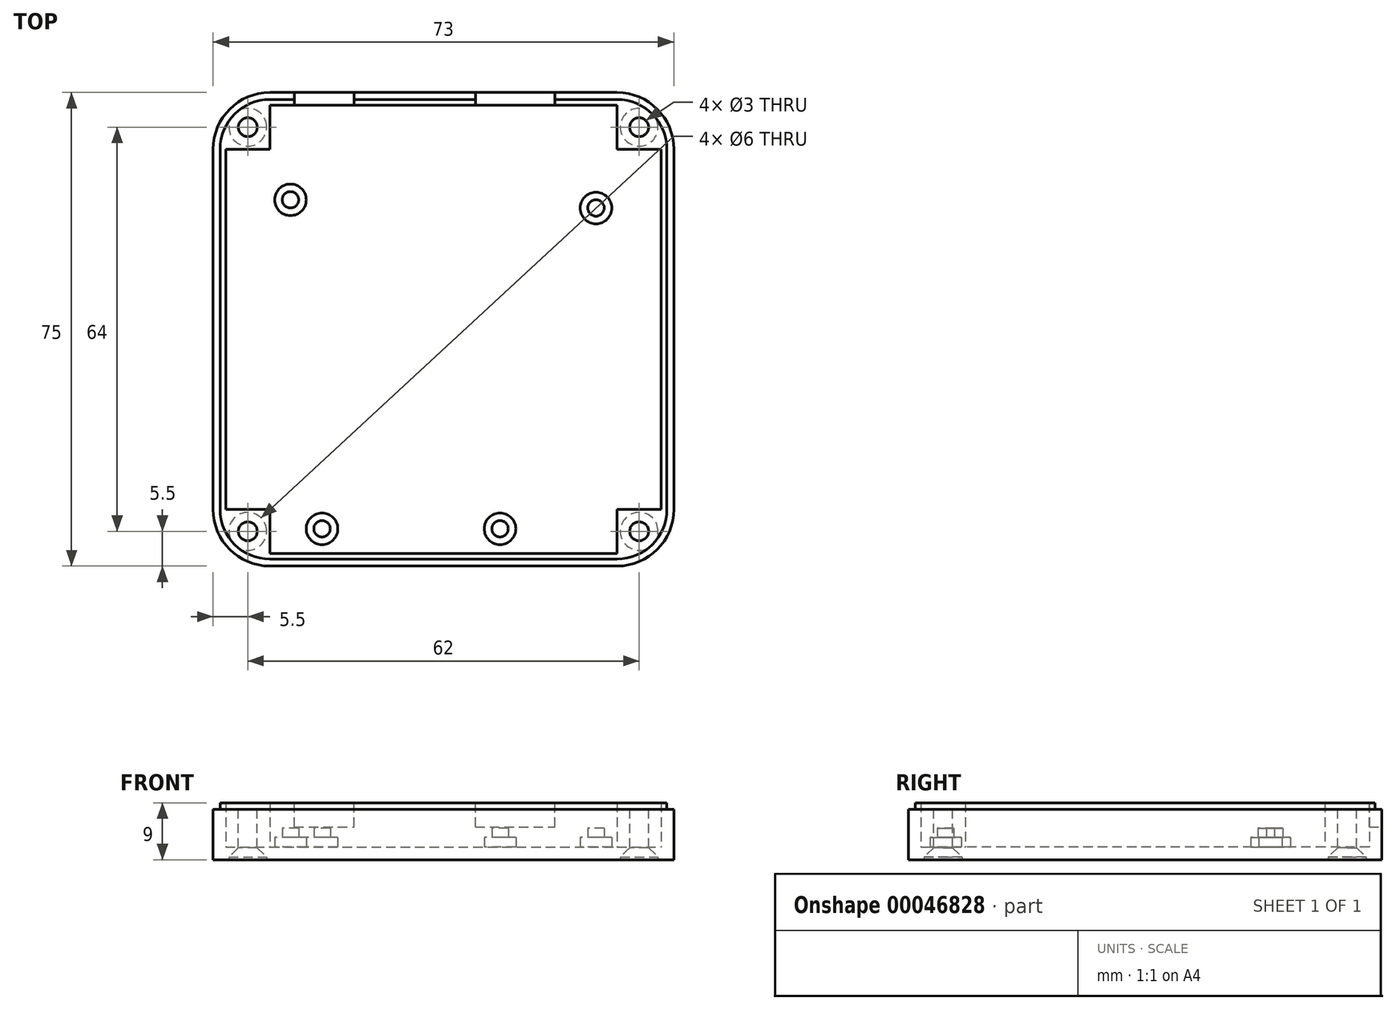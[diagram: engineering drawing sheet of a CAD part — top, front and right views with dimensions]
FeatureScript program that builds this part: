
annotation { "Feature Type Name" : "Feature", "Feature Type Description" : "" }
export const myFeature = defineFeature(function(context is Context, id is Id, definition is map)
    precondition{}
    {
        {
            var Q0;
            Q0=qCreatedBy(makeId("Top.planeOp"),FACE);
            var sketch = newSketch(context, id + "F0", { "sketchPlane" : qUnion([Q0])});
            skLineSegment(sketch, "E0.bottom", {"start": v(-27.5, 38.5) * mm, "end": v(27.5, 38.5) * mm});
            skLineSegment(sketch, "E0.top", {"start": v(-27.5, -36.5) * mm, "end": v(27.5, -36.5) * mm});
            skLineSegment(sketch, "E0.left", {"start": v(-36.5, 29.5) * mm, "end": v(-36.5, -27.5) * mm});
            skLineSegment(sketch, "E0.right", {"start": v(36.5, 29.5) * mm, "end": v(36.5, -27.5) * mm});
            skPoint(sketch, "E1.visualSharp", {"position": v(-36.5, 38.5) * mm});
            skArc(sketch, "E1.filletArc", {"start": v(-27.5, 38.5) * mm, "mid": v(-33.86, 35.86) * mm, "end": v(-36.5, 29.5) * mm});
            skPoint(sketch, "E2.visualSharp", {"position": v(36.5, 38.5) * mm});
            skArc(sketch, "E2.filletArc", {"start": v(36.5, 29.5) * mm, "mid": v(33.86, 35.86) * mm, "end": v(27.5, 38.5) * mm});
            skPoint(sketch, "E3.visualSharp", {"position": v(36.5, -36.5) * mm});
            skArc(sketch, "E3.filletArc", {"start": v(27.5, -36.5) * mm, "mid": v(33.86, -33.86) * mm, "end": v(36.5, -27.5) * mm});
            skPoint(sketch, "E4.visualSharp", {"position": v(-36.5, -36.5) * mm});
            skArc(sketch, "E4.filletArc", {"start": v(-36.5, -27.5) * mm, "mid": v(-33.86, -33.86) * mm, "end": v(-27.5, -36.5) * mm});
            skSolve(sketch);
        }
        {
            var Q0;
            Q0 = qSketchRegion(id + "F0", true);
            extrude(context, id + "F1", {"entities" : qUnion([Q0]), "depth" : 2 * mm});
        }
        {
            var Q0;
            Q0=makeQuery(id+"F1.opExtrude","CAP_FACE",FACE,{"disambiguationData":[OSD([sQuery(id+"F0.wireOp",EDGE,"E0.bottom"),sQuery(id+"F0.wireOp",EDGE,"E0.top"),sQuery(id+"F0.wireOp",EDGE,"E0.left"),sQuery(id+"F0.wireOp",EDGE,"E0.right")])],"isStart":false});
            var sketch = newSketch(context, id + "F2", { "sketchPlane" : qUnion([Q0])});
            skCircle(sketch, "E5", {"center": v(-19.24, -30.6) * mm, "radius": 2.5 * mm});
            skCircle(sketch, "E6", {"center": v(8.96, -30.6) * mm, "radius": 2.5 * mm});
            skCircle(sketch, "E7", {"center": v(24.16, 20.2) * mm, "radius": 2.5 * mm});
            skCircle(sketch, "E8", {"center": v(-24.24, 21.5) * mm, "radius": 2.5 * mm});
            skSolve(sketch);
        }
        {
            var Q0;
            Q0 = qSketchRegion(id + "F2", true);
            extrude(context, id + "F3", {"entities" : qUnion([Q0]), "operationType" : NewBodyOperationType.ADD, "depth" : 1.5 * mm});
        }
        {
            var Q0;
            Q0=makeQuery(id+"F3.opExtrude","CAP_FACE",FACE,{"disambiguationData":[OSD([sQuery(id+"F2.wireOp",EDGE,"E8")])],"isStart":false});
            var sketch = newSketch(context, id + "F4", { "sketchPlane" : qUnion([Q0])});
            skCircle(sketch, "E9", {"center": v(-19.24, -30.6) * mm, "radius": 1.3 * mm});
            skCircle(sketch, "E10", {"center": v(8.96, -30.6) * mm, "radius": 1.3 * mm});
            skCircle(sketch, "E11", {"center": v(24.16, 20.2) * mm, "radius": 1.3 * mm});
            skCircle(sketch, "E12", {"center": v(-24.24, 21.5) * mm, "radius": 1.3 * mm});
            skSolve(sketch);
        }
        {
            var Q0;
            Q0 = qSketchRegion(id + "F4", true);
            extrude(context, id + "F5", {"entities" : qUnion([Q0]), "operationType" : NewBodyOperationType.ADD, "depth" : 1.5 * mm});
        }
        {
            var Q0;
            Q0=makeQuery(id+"F1.opExtrude","CAP_FACE",FACE,{"disambiguationData":[OSD([sQuery(id+"F0.wireOp",EDGE,"E0.bottom"),sQuery(id+"F0.wireOp",EDGE,"E0.top"),sQuery(id+"F0.wireOp",EDGE,"E0.left"),sQuery(id+"F0.wireOp",EDGE,"E0.right"),sQuery(id+"F0.wireOp",EDGE,"E1.filletArc"),sQuery(id+"F0.wireOp",EDGE,"E2.filletArc"),sQuery(id+"F0.wireOp",EDGE,"E3.filletArc"),sQuery(id+"F0.wireOp",EDGE,"E4.filletArc")])],"isStart":false});
            var sketch = newSketch(context, id + "F6", { "sketchPlane" : qUnion([Q0])});
            skLineSegment(sketch, "E13.bottom", {"start": v(-27.5, 38.5) * mm, "end": v(27.5, 38.5) * mm});
            skLineSegment(sketch, "E13.top", {"start": v(-27.5, -36.5) * mm, "end": v(27.5, -36.5) * mm});
            skLineSegment(sketch, "E13.left", {"start": v(-36.5, 29.5) * mm, "end": v(-36.5, -27.5) * mm});
            skLineSegment(sketch, "E13.right", {"start": v(36.5, 29.5) * mm, "end": v(36.5, -27.5) * mm});
            skPoint(sketch, "E14.visualSharp", {"position": v(-36.5, 38.5) * mm});
            skArc(sketch, "E14.filletArc", {"start": v(-27.5, 38.5) * mm, "mid": v(-33.86, 35.86) * mm, "end": v(-36.5, 29.5) * mm});
            skPoint(sketch, "E15.visualSharp", {"position": v(36.5, 38.5) * mm});
            skArc(sketch, "E15.filletArc", {"start": v(36.5, 29.5) * mm, "mid": v(33.86, 35.86) * mm, "end": v(27.5, 38.5) * mm});
            skPoint(sketch, "E16.visualSharp", {"position": v(36.5, -36.5) * mm});
            skArc(sketch, "E16.filletArc", {"start": v(27.5, -36.5) * mm, "mid": v(33.86, -33.86) * mm, "end": v(36.5, -27.5) * mm});
            skPoint(sketch, "E17.visualSharp", {"position": v(-36.5, -36.5) * mm});
            skArc(sketch, "E17.filletArc", {"start": v(-36.5, -27.5) * mm, "mid": v(-33.86, -33.86) * mm, "end": v(-27.5, -36.5) * mm});
            skLineSegment(sketch, "E18", {"start": v(-27.5, 36.5) * mm, "end": v(27.5, 36.5) * mm});
            skLineSegment(sketch, "E19", {"start": v(-34.5, 29.5) * mm, "end": v(-34.5, -27.5) * mm});
            skLineSegment(sketch, "E20", {"start": v(-27.5, -34.5) * mm, "end": v(27.5, -34.5) * mm});
            skLineSegment(sketch, "E21", {"start": v(34.5, 29.5) * mm, "end": v(34.5, -27.5) * mm});
            skLineSegment(sketch, "E22", {"start": v(-34.5, 29.5) * mm, "end": v(-27.5, 29.5) * mm});
            skLineSegment(sketch, "E23", {"start": v(-27.5, 36.5) * mm, "end": v(-27.5, 29.5) * mm});
            skLineSegment(sketch, "E24", {"start": v(27.5, 36.5) * mm, "end": v(27.5, 29.5) * mm});
            skLineSegment(sketch, "E25", {"start": v(27.5, 29.5) * mm, "end": v(34.5, 29.5) * mm});
            skLineSegment(sketch, "E26", {"start": v(-34.5, -27.5) * mm, "end": v(-27.5, -27.5) * mm});
            skLineSegment(sketch, "E27", {"start": v(-27.5, -34.5) * mm, "end": v(-27.5, -27.5) * mm});
            skLineSegment(sketch, "E28", {"start": v(27.5, -34.5) * mm, "end": v(27.5, -27.5) * mm});
            skLineSegment(sketch, "E29", {"start": v(27.5, -27.5) * mm, "end": v(34.5, -27.5) * mm});
            skSolve(sketch);
        }
        {
            var Q0;
            Q0 = qSketchRegion(id + "F6", true);
            extrude(context, id + "F7", {"entities" : qUnion([Q0]), "operationType" : NewBodyOperationType.ADD, "depth" : 7 * mm});
        }
        {
            var Q0;
            Q0=makeQuery(id+"F7.opExtrude","CAP_FACE",FACE,{"disambiguationData":[OSD([sQuery(id+"F6.wireOp",EDGE,"E13.bottom"),sQuery(id+"F6.wireOp",EDGE,"E13.top"),sQuery(id+"F6.wireOp",EDGE,"E13.left"),sQuery(id+"F6.wireOp",EDGE,"E13.right"),sQuery(id+"F6.wireOp",EDGE,"E14.filletArc"),sQuery(id+"F6.wireOp",EDGE,"E15.filletArc"),sQuery(id+"F6.wireOp",EDGE,"E16.filletArc"),sQuery(id+"F6.wireOp",EDGE,"E17.filletArc"),sQuery(id+"F6.wireOp",EDGE,"E18"),sQuery(id+"F6.wireOp",EDGE,"E19"),sQuery(id+"F6.wireOp",EDGE,"E20"),sQuery(id+"F6.wireOp",EDGE,"E21"),sQuery(id+"F6.wireOp",EDGE,"E22"),sQuery(id+"F6.wireOp",EDGE,"E23"),sQuery(id+"F6.wireOp",EDGE,"E24"),sQuery(id+"F6.wireOp",EDGE,"E25"),sQuery(id+"F6.wireOp",EDGE,"E26"),sQuery(id+"F6.wireOp",EDGE,"E27"),sQuery(id+"F6.wireOp",EDGE,"E28"),sQuery(id+"F6.wireOp",EDGE,"E29")])],"isStart":false});
            var sketch = newSketch(context, id + "F8", { "sketchPlane" : qUnion([Q0])});
            skCircle(sketch, "E30", {"center": v(-31, 33) * mm, "radius": 1.5 * mm});
            skCircle(sketch, "E31", {"center": v(31, 33) * mm, "radius": 1.5 * mm});
            skCircle(sketch, "E32", {"center": v(-31, -31) * mm, "radius": 1.5 * mm});
            skCircle(sketch, "E33", {"center": v(31, -31) * mm, "radius": 1.5 * mm});
            skSolve(sketch);
        }
        {
            var Q0;
            Q0 = qSketchRegion(id + "F8", true);
            extrude(context, id + "F9", {"entities" : qUnion([Q0]), "operationType" : NewBodyOperationType.REMOVE, "oppositeDirection" : true, "depth" : 10 * mm});
        }
        {
            var Q0;
            Q0=makeQuery(id+"F7.opExtrude","CAP_FACE",FACE,{"disambiguationData":[OSD([sQuery(id+"F6.wireOp",EDGE,"E13.bottom"),sQuery(id+"F6.wireOp",EDGE,"E13.top"),sQuery(id+"F6.wireOp",EDGE,"E13.left"),sQuery(id+"F6.wireOp",EDGE,"E13.right"),sQuery(id+"F6.wireOp",EDGE,"E14.filletArc"),sQuery(id+"F6.wireOp",EDGE,"E15.filletArc"),sQuery(id+"F6.wireOp",EDGE,"E16.filletArc"),sQuery(id+"F6.wireOp",EDGE,"E17.filletArc"),sQuery(id+"F6.wireOp",EDGE,"E18"),sQuery(id+"F6.wireOp",EDGE,"E19"),sQuery(id+"F6.wireOp",EDGE,"E20"),sQuery(id+"F6.wireOp",EDGE,"E21"),sQuery(id+"F6.wireOp",EDGE,"E22"),sQuery(id+"F6.wireOp",EDGE,"E23"),sQuery(id+"F6.wireOp",EDGE,"E24"),sQuery(id+"F6.wireOp",EDGE,"E25"),sQuery(id+"F6.wireOp",EDGE,"E26"),sQuery(id+"F6.wireOp",EDGE,"E27"),sQuery(id+"F6.wireOp",EDGE,"E28"),sQuery(id+"F6.wireOp",EDGE,"E29")])],"isStart":false});
            var sketch = newSketch(context, id + "F10", { "sketchPlane" : qUnion([Q0])});
            skLineSegment(sketch, "E34.bottom", {"start": v(17.66, 36.5) * mm, "end": v(5.06, 36.5) * mm});
            skLineSegment(sketch, "E34.top", {"start": v(17.66, 38.5) * mm, "end": v(5.06, 38.5) * mm});
            skLineSegment(sketch, "E34.left", {"start": v(17.66, 36.5) * mm, "end": v(17.66, 38.5) * mm});
            skLineSegment(sketch, "E34.right", {"start": v(5.06, 36.5) * mm, "end": v(5.06, 38.5) * mm});
            skLineSegment(sketch, "E35.bottom", {"start": v(-14.14, 36.5) * mm, "end": v(-23.64, 36.5) * mm});
            skLineSegment(sketch, "E35.top", {"start": v(-14.14, 38.5) * mm, "end": v(-23.64, 38.5) * mm});
            skLineSegment(sketch, "E35.left", {"start": v(-14.14, 36.5) * mm, "end": v(-14.14, 38.5) * mm});
            skLineSegment(sketch, "E35.right", {"start": v(-23.64, 36.5) * mm, "end": v(-23.64, 38.5) * mm});
            skSolve(sketch);
        }
        {
            var Q0;
            Q0 = qSketchRegion(id + "F10", true);
            extrude(context, id + "F11", {"entities" : qUnion([Q0]), "operationType" : NewBodyOperationType.REMOVE, "oppositeDirection" : true, "depth" : 3.8 * mm});
        }
        {
            var Q0;
            Q0=makeQuery(id+"F1.opExtrude","CAP_FACE",FACE,{"disambiguationData":[OSD([sQuery(id+"F0.wireOp",EDGE,"E0.bottom"),sQuery(id+"F0.wireOp",EDGE,"E0.top"),sQuery(id+"F0.wireOp",EDGE,"E0.left"),sQuery(id+"F0.wireOp",EDGE,"E0.right"),sQuery(id+"F0.wireOp",EDGE,"E1.filletArc"),sQuery(id+"F0.wireOp",EDGE,"E2.filletArc"),sQuery(id+"F0.wireOp",EDGE,"E3.filletArc"),sQuery(id+"F0.wireOp",EDGE,"E4.filletArc")])],"isStart":true});
            var sketch = newSketch(context, id + "F12", { "sketchPlane" : qUnion([Q0])});
            skCircle(sketch, "E36", {"center": v(31, -33) * mm, "radius": 3 * mm});
            skCircle(sketch, "E37", {"center": v(-31, -33) * mm, "radius": 3 * mm});
            skCircle(sketch, "E38", {"center": v(-31, 31) * mm, "radius": 3 * mm});
            skCircle(sketch, "E39", {"center": v(31, 31) * mm, "radius": 3 * mm});
            skSolve(sketch);
        }
        {
            var Q0;
            Q0 = qSketchRegion(id + "F12", true);
            extrude(context, id + "F13", {"entities" : qUnion([Q0]), "operationType" : NewBodyOperationType.REMOVE, "oppositeDirection" : true, "depth" : .4 * mm});
        }
        {
            var Q0;
            Q0=makeQuery(id+"F13.boolean.opBoolean","INTERSECT",EDGE,{"derivedFrom":[makeQuery(id+"F9.boolean.opBoolean","COPY",FACE,{"derivedFrom":makeQuery(id+"F9.opExtrude","SWEPT_FACE",FACE,{"disambiguationData":[OSD([sQuery(id+"F8.wireOp",EDGE,"E31")])]})}),makeQuery(id+"F13.opExtrude","CAP_FACE",FACE,{"disambiguationData":[OSD([sQuery(id+"F12.wireOp",EDGE,"E36")])],"isStart":false})]});
            var Q1;
            Q1=makeQuery(id+"F13.boolean.opBoolean","INTERSECT",EDGE,{"derivedFrom":[makeQuery(id+"F9.boolean.opBoolean","COPY",FACE,{"derivedFrom":makeQuery(id+"F9.opExtrude","SWEPT_FACE",FACE,{"disambiguationData":[OSD([sQuery(id+"F8.wireOp",EDGE,"E30")])]})}),makeQuery(id+"F13.opExtrude","CAP_FACE",FACE,{"disambiguationData":[OSD([sQuery(id+"F12.wireOp",EDGE,"E37")])],"isStart":false})]});
            var Q2;
            Q2=makeQuery(id+"F13.boolean.opBoolean","INTERSECT",EDGE,{"derivedFrom":[makeQuery(id+"F9.boolean.opBoolean","COPY",FACE,{"derivedFrom":makeQuery(id+"F9.opExtrude","SWEPT_FACE",FACE,{"disambiguationData":[OSD([sQuery(id+"F8.wireOp",EDGE,"E33")])]})}),makeQuery(id+"F13.opExtrude","CAP_FACE",FACE,{"disambiguationData":[OSD([sQuery(id+"F12.wireOp",EDGE,"E39")])],"isStart":false})]});
            var Q3;
            Q3=makeQuery(id+"F13.boolean.opBoolean","INTERSECT",EDGE,{"derivedFrom":[makeQuery(id+"F9.boolean.opBoolean","COPY",FACE,{"derivedFrom":makeQuery(id+"F9.opExtrude","SWEPT_FACE",FACE,{"disambiguationData":[OSD([sQuery(id+"F8.wireOp",EDGE,"E32")])]})}),makeQuery(id+"F13.opExtrude","CAP_FACE",FACE,{"disambiguationData":[OSD([sQuery(id+"F12.wireOp",EDGE,"E38")])],"isStart":false})]});
            chamfer(context, id + "F14", {"entities" : qUnion([Q0, Q1, Q2, Q3]), "width" : 1.5 * mm, "tangentPropagation" : true});
        }
        {
            var Q0;
            {var subQ0=sQuery(id+"F6.wireOp",EDGE,"E13.bottom");var subQ1=sQuery(id+"F6.wireOp",EDGE,"E13.top");var subQ2=sQuery(id+"F6.wireOp",EDGE,"E13.left");var subQ3=sQuery(id+"F6.wireOp",EDGE,"E13.right");var subQ4=sQuery(id+"F6.wireOp",EDGE,"E14.filletArc");var subQ5=sQuery(id+"F6.wireOp",EDGE,"E15.filletArc");var subQ6=sQuery(id+"F6.wireOp",EDGE,"E16.filletArc");var subQ7=sQuery(id+"F6.wireOp",EDGE,"E17.filletArc");var subQ8=sQuery(id+"F6.wireOp",EDGE,"E18");var subQ9=sQuery(id+"F6.wireOp",EDGE,"E19");var subQ10=sQuery(id+"F6.wireOp",EDGE,"E20");var subQ11=sQuery(id+"F6.wireOp",EDGE,"E21");var subQ12=sQuery(id+"F6.wireOp",EDGE,"E22");var subQ13=sQuery(id+"F6.wireOp",EDGE,"E23");var subQ14=sQuery(id+"F6.wireOp",EDGE,"E24");var subQ15=sQuery(id+"F6.wireOp",EDGE,"E25");var subQ16=sQuery(id+"F6.wireOp",EDGE,"E26");var subQ17=sQuery(id+"F6.wireOp",EDGE,"E27");var subQ18=sQuery(id+"F6.wireOp",EDGE,"E28");var subQ19=sQuery(id+"F6.wireOp",EDGE,"E29");Q0=makeQuery(id+"F11.boolean.opBoolean","SPLIT",FACE,{"disambiguationData":[TD([makeQuery(id+"F1.opExtrude","SWEPT_FACE",FACE,{"disambiguationData":[OSD([sQuery(id+"F0.wireOp",EDGE,"E0.top")])]})])],"derivedFrom":makeQuery(id+"F7.opExtrude","CAP_FACE",FACE,{"disambiguationData":[OSD([subQ0,subQ1,subQ2,subQ3,subQ4,subQ5,subQ6,subQ7,subQ8,subQ9,subQ10,subQ11,subQ12,subQ13,subQ14,subQ15,subQ16,subQ17,subQ18,subQ19])],"isStart":false})});}
            var sketch = newSketch(context, id + "F15", { "sketchPlane" : qUnion([Q0])});
            skLineSegment(sketch, "E40.0", {"start": v(-27.5, 38.5) * mm, "end": v(-23.64, 38.5) * mm});
            skArc(sketch, "E40.1", {"start": v(-27.5, 38.5) * mm, "mid": v(-33.86, 35.86) * mm, "end": v(-36.5, 29.5) * mm});
            skLineSegment(sketch, "E40.2", {"start": v(-36.5, 29.5) * mm, "end": v(-36.5, -27.5) * mm});
            skArc(sketch, "E40.3", {"start": v(-36.5, -27.5) * mm, "mid": v(-33.86, -33.86) * mm, "end": v(-27.5, -36.5) * mm});
            skLineSegment(sketch, "E40.4", {"start": v(-27.5, -36.5) * mm, "end": v(27.5, -36.5) * mm});
            skArc(sketch, "E40.5", {"start": v(27.5, -36.5) * mm, "mid": v(33.86, -33.86) * mm, "end": v(36.5, -27.5) * mm});
            skLineSegment(sketch, "E40.6", {"start": v(36.5, 29.5) * mm, "end": v(36.5, -27.5) * mm});
            skArc(sketch, "E40.7", {"start": v(36.5, 29.5) * mm, "mid": v(33.86, 35.86) * mm, "end": v(27.5, 38.5) * mm});
            skLineSegment(sketch, "E40.8", {"start": v(17.66, 38.5) * mm, "end": v(27.5, 38.5) * mm});
            skLineSegment(sketch, "E40.9", {"start": v(-14.14, 38.5) * mm, "end": v(5.06, 38.5) * mm});
            skLineSegment(sketch, "E41.top", {"start": v(-14.14, 37.4) * mm, "end": v(5.06, 37.4) * mm});
            skLineSegment(sketch, "E41.left", {"start": v(-14.14, 38.5) * mm, "end": v(-14.14, 37.4) * mm});
            skLineSegment(sketch, "E41.right", {"start": v(5.06, 38.5) * mm, "end": v(5.06, 37.4) * mm});
            skLineSegment(sketch, "E42", {"start": v(-35.4, 29.5) * mm, "end": v(-35.4, -27.5) * mm});
            skLineSegment(sketch, "E43", {"start": v(35.4, 29.5) * mm, "end": v(35.4, -27.5) * mm});
            skLineSegment(sketch, "E44", {"start": v(-27.5, -35.4) * mm, "end": v(27.5, -35.4) * mm});
            skLineSegment(sketch, "E45", {"start": v(-27.5, 37.4) * mm, "end": v(-23.64, 37.4) * mm});
            skLineSegment(sketch, "E46", {"start": v(-23.64, 37.4) * mm, "end": v(-23.64, 38.5) * mm});
            skArc(sketch, "E47", {"start": v(-27.5, 37.4) * mm, "mid": v(-33.09, 35.09) * mm, "end": v(-35.4, 29.5) * mm});
            skLineSegment(sketch, "E48", {"start": v(27.5, 37.4) * mm, "end": v(17.66, 37.4) * mm});
            skLineSegment(sketch, "E49", {"start": v(17.66, 38.5) * mm, "end": v(17.66, 37.4) * mm});
            skArc(sketch, "E50", {"start": v(35.4, 29.5) * mm, "mid": v(33.09, 35.09) * mm, "end": v(27.5, 37.4) * mm});
            skArc(sketch, "E51", {"start": v(27.5, -35.4) * mm, "mid": v(33.09, -33.09) * mm, "end": v(35.4, -27.5) * mm});
            skArc(sketch, "E52", {"start": v(-35.4, -27.5) * mm, "mid": v(-33.09, -33.09) * mm, "end": v(-27.5, -35.4) * mm});
            skSolve(sketch);
        }
        {
            var Q0;
            Q0 = qSketchRegion(id + "F15", true);
            extrude(context, id + "F16", {"entities" : qUnion([Q0]), "operationType" : NewBodyOperationType.REMOVE, "oppositeDirection" : true, "depth" : 1 * mm});
        }
    });
